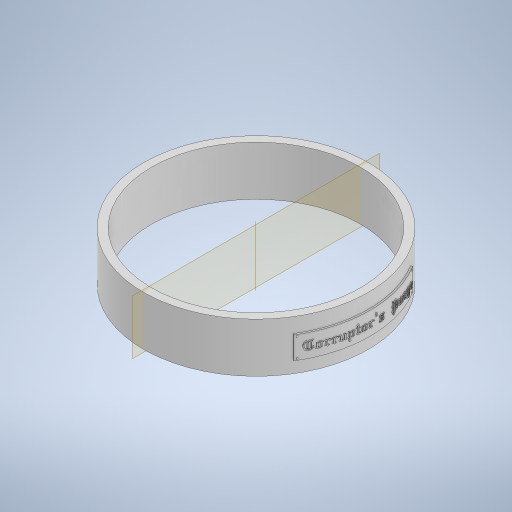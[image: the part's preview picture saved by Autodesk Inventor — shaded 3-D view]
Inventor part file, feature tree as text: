
AUTODESK INVENTOR PART (.ipt)
format: ipt  version: 2023 (Build 270158000, 158)  size: 4,565,504 bytes
history: native  units: in
note: dims shown in document units (in); Inventor stores cm internally (conversion verified against a paired STEP export)
features: emboss x3, pattern_circular x3, other x2, extrude x1, plane x1, fillet x1, sketch x1
ambient origin geometry x8: Origin, YZ Plane, XZ Plane, XY Plane, X Axis, Y Axis, Z Axis, Center Point
bodies: Solid1 (feature_tree)
feature tree (12):
  extrude  "Extrusion1"  Depth=0.3937in
  plane  "Work Plane1"
  other  "Text"
  emboss  "Emboss4"
  emboss  "Emboss5"
  emboss  "Emboss6"
  fillet  "Rivots"  Radius=0.8661in
  pattern_circular  "Circular Pattern1"  Count=6  [1 undecoded]
  pattern_circular  "Circular Pattern2"  [2 undecoded]
  pattern_circular  "Circular Pattern3"  [2 undecoded]
  sketch  "Sketch1"  dims[d0=3.937in d1=3.6614in d2=0.8661in d3=0.0in d4=2.3622in d6=0.4546in d10=0.0in d11=0.3937in d12=2.1654in d19=0.0in d20=0.0in d21=0.0295in d22=0.0in d23=0.0197in d24=0.0in d25=0.0295in d26=0.0295in d27=0.0295in d28=0.0157in d29=0.0in d30=0.0138in d31=0.7874in d32=360.0deg d34=0.7874in d35=360.0deg d37=0.7874in d38=360.0deg d33=0.0in]
  other  "NamePlate"
note: 5 required parameter values undecoded (feature->parameter linkage not recoverable at this tier; creation-order binding heuristic only, values carry confidence <= 0.55)
